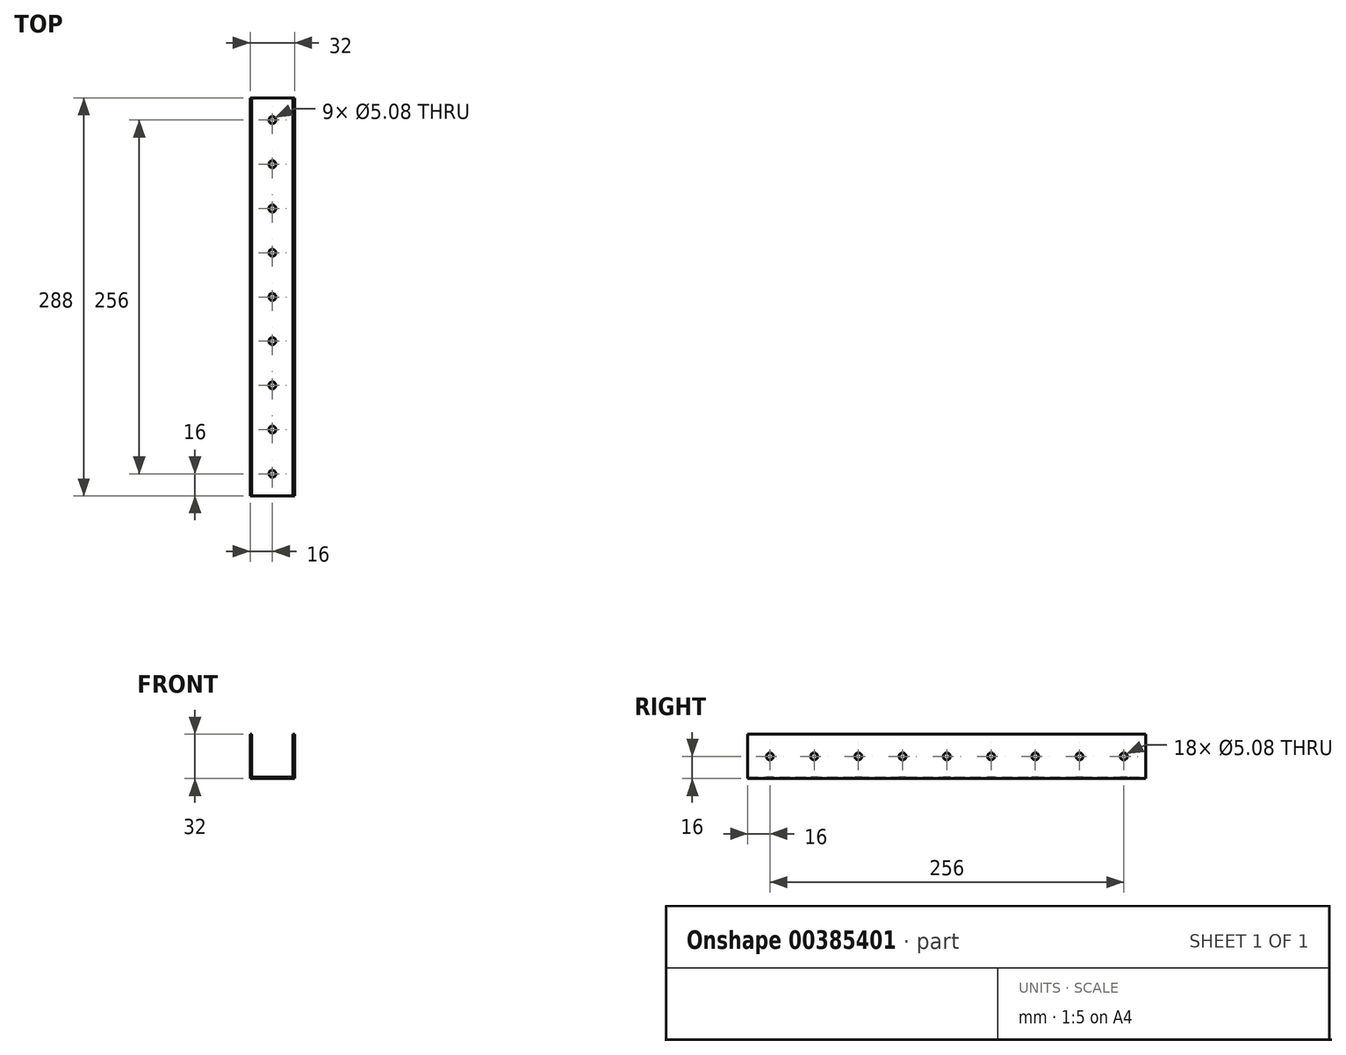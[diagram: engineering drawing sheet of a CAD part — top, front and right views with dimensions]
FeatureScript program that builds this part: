
annotation { "Feature Type Name" : "Feature", "Feature Type Description" : "" }
export const myFeature = defineFeature(function(context is Context, id is Id, definition is map)
    precondition{}
    {
        {
            var Q0;
            Q0=qCreatedBy(makeId("Front.planeOp"),FACE);
            var sketch = newSketch(context, id + "F0", { "sketchPlane" : qUnion([Q0])});
            skLineSegment(sketch, "E0", {"start": v(-16, 15.75) * mm, "end": v(-16, -16.25) * mm});
            skLineSegment(sketch, "E1", {"start": v(-16, -16.25) * mm, "end": v(16, -16.25) * mm});
            skLineSegment(sketch, "E2", {"start": v(16, -16.25) * mm, "end": v(16, 15.75) * mm});
            skLineSegment(sketch, "E3", {"start": v(16, 15.75) * mm, "end": v(15, 15.75) * mm});
            skLineSegment(sketch, "E4", {"start": v(15, 15.75) * mm, "end": v(15, -15.25) * mm});
            skLineSegment(sketch, "E5", {"start": v(15, -15.25) * mm, "end": v(-15, -15.25) * mm});
            skLineSegment(sketch, "E6", {"start": v(-15, -15.25) * mm, "end": v(-15, 15.75) * mm});
            skLineSegment(sketch, "E7", {"start": v(-15, 15.75) * mm, "end": v(-16, 15.75) * mm});
            skSolve(sketch);
        }
        {
            var Q0;
            Q0=qSketchRegion(id+"F0",true);
            extrude(context, id + "F1", {"entities" : qUnion([Q0]), "depth" : 288 * mm});
        }
        {
            var Q0;
            Q0=makeQuery(id+"F1.opExtrude","SWEPT_FACE",FACE,{"disambiguationData":[OSD([sQuery(id+"F0.wireOp",EDGE,"E0")])]});
            var sketch = newSketch(context, id + "F2", { "sketchPlane" : qUnion([Q0])});
            skPoint(sketch, "E8", {"position": v(16, -0.25) * mm});
            skCircle(sketch, "E9", {"center": v(16, -0.25) * mm, "radius": 2.54 * mm});
            skCircle(sketch, "E10.1.0.0", {"center": v(48, -0.25) * mm, "radius": 2.54 * mm});
            skCircle(sketch, "E10.2.0.0", {"center": v(80, -0.25) * mm, "radius": 2.54 * mm});
            skCircle(sketch, "E10.3.0.0", {"center": v(112, -0.25) * mm, "radius": 2.54 * mm});
            skCircle(sketch, "E10.4.0.0", {"center": v(144, -0.25) * mm, "radius": 2.54 * mm});
            skCircle(sketch, "E10.5.0.0", {"center": v(176, -0.25) * mm, "radius": 2.54 * mm});
            skCircle(sketch, "E10.6.0.0", {"center": v(208, -0.25) * mm, "radius": 2.54 * mm});
            skCircle(sketch, "E10.7.0.0", {"center": v(240, -0.25) * mm, "radius": 2.54 * mm});
            skCircle(sketch, "E10.8.0.0", {"center": v(272, -0.25) * mm, "radius": 2.54 * mm});
            skLineSegment(sketch, "E10.direction1", {"start": v(16, -0.25) * mm, "end": v(48, -0.25) * mm, "construction": true});
            skSolve(sketch);
        }
        {
            var Q0;
            Q0=qSketchRegion(id+"F2",true);
            extrude(context, id + "F3", {"entities" : qUnion([Q0]), "operationType" : NewBodyOperationType.REMOVE, "oppositeDirection" : true, "depth" : 50.8 * mm});
        }
        {
            var Q0;
            Q0=makeQuery(id+"F1.opExtrude","SWEPT_FACE",FACE,{"disambiguationData":[OSD([sQuery(id+"F0.wireOp",EDGE,"E1")])]});
            var sketch = newSketch(context, id + "F4", { "sketchPlane" : qUnion([Q0])});
            skPoint(sketch, "E11", {"position": v(0, 272) * mm});
            skCircle(sketch, "E12", {"center": v(0, 272) * mm, "radius": 2.54 * mm});
            skCircle(sketch, "E13.0.1.0", {"center": v(0, 240) * mm, "radius": 2.54 * mm});
            skCircle(sketch, "E13.0.2.0", {"center": v(0, 208) * mm, "radius": 2.54 * mm});
            skCircle(sketch, "E13.0.3.0", {"center": v(0, 176) * mm, "radius": 2.54 * mm});
            skCircle(sketch, "E13.0.4.0", {"center": v(0, 144) * mm, "radius": 2.54 * mm});
            skCircle(sketch, "E13.0.5.0", {"center": v(0, 112) * mm, "radius": 2.54 * mm});
            skCircle(sketch, "E13.0.6.0", {"center": v(0, 80) * mm, "radius": 2.54 * mm});
            skCircle(sketch, "E13.0.7.0", {"center": v(0, 48) * mm, "radius": 2.54 * mm});
            skCircle(sketch, "E13.0.8.0", {"center": v(0, 16) * mm, "radius": 2.54 * mm});
            skLineSegment(sketch, "E13.direction1", {"start": v(0, 272) * mm, "end": v(41.8, 272) * mm, "construction": true});
            skLineSegment(sketch, "E13.direction2", {"start": v(0, 272) * mm, "end": v(0, 240) * mm, "construction": true});
            skSolve(sketch);
        }
        {
            var Q0;
            Q0=qSketchRegion(id+"F4",true);
            extrude(context, id + "F5", {"entities" : qUnion([Q0]), "operationType" : NewBodyOperationType.REMOVE, "oppositeDirection" : true, "depth" : 25.4 * mm});
        }
    });
